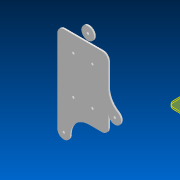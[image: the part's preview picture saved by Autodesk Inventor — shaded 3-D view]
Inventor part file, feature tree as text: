
AUTODESK INVENTOR PART (.ipt)
format: ipt  version: 2022 (Build 260153000, 153)  size: 141,824 bytes
history: native  units: in
note: dims shown in document units (in); Inventor stores cm internally (conversion verified against a paired STEP export)
features: sketch x1, extrude x1, hole x1
ambient origin geometry x8: Origin, YZ Plane, XZ Plane, XY Plane, X Axis, Y Axis, Z Axis, Center Point
bodies: Solid1 (feature_tree)
feature tree (3):
  sketch  "Sketch1"  dims[d0=1.5in d1=3.0in d2=1.25in d3=1.25in d4=0.125in d5=0.0in d6=0.18in d7=0.75in d8=0.375in d9=0.25in d10=0.5635in d11=1.0in d12=0.8108in d13=1.0in d20=0.5in d21=3.0in d22=1.5in d23=1.2931in]
  extrude  "Extrusion1"  Depth=1.2931in
  hole  "Hole1"  [1 undecoded]
note: 1 required parameter value undecoded (feature->parameter linkage not recoverable at this tier; creation-order binding heuristic only, values carry confidence <= 0.55)
